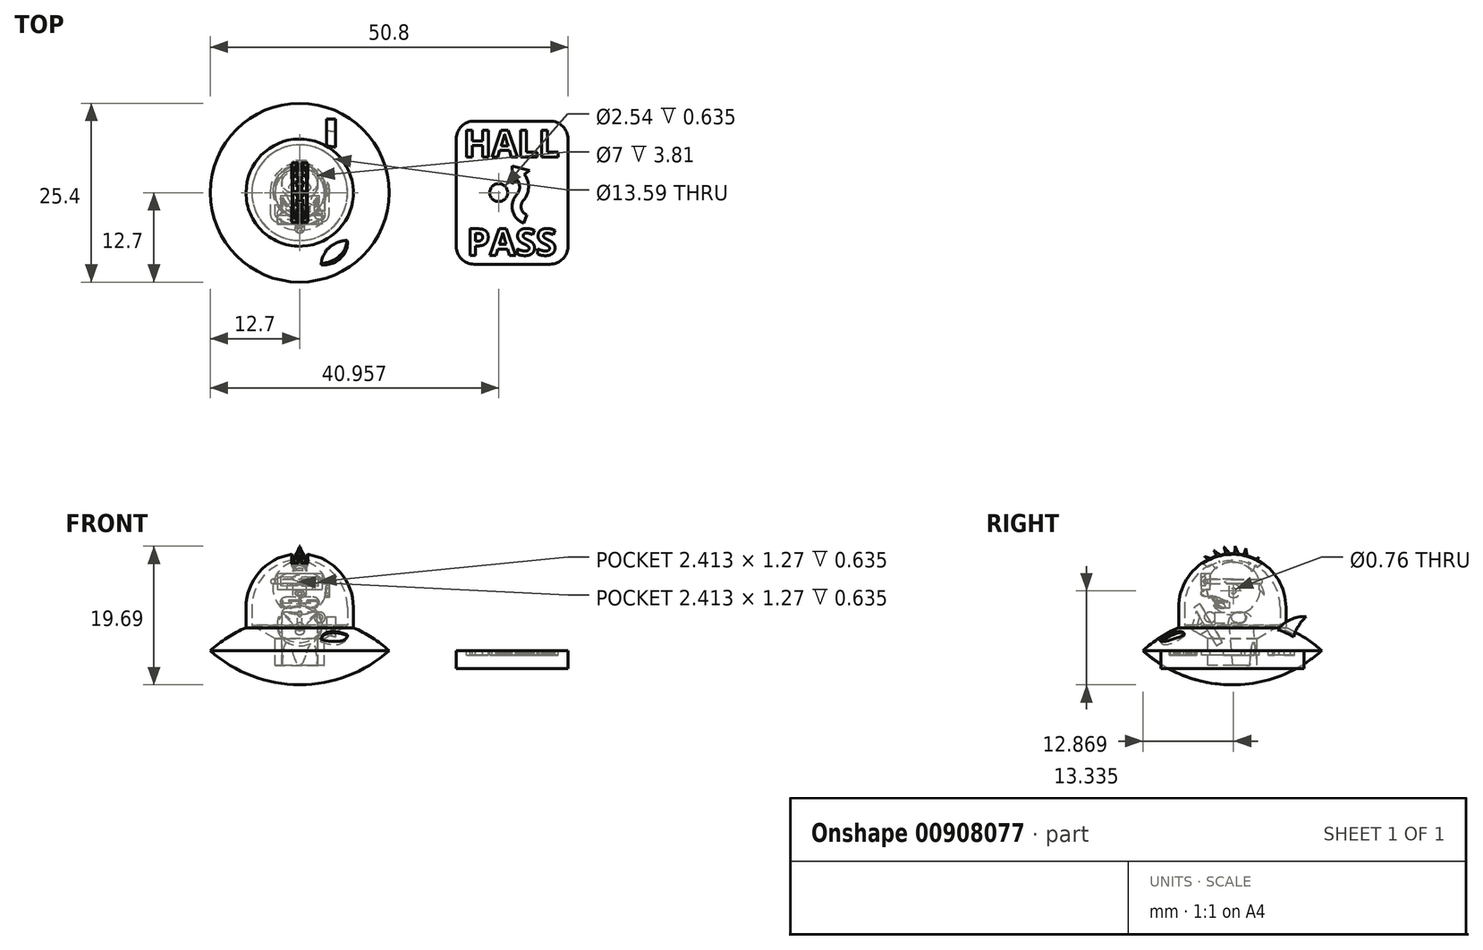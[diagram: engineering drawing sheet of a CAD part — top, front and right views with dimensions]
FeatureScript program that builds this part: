
annotation { "Feature Type Name" : "Feature", "Feature Type Description" : "" }
export const myFeature = defineFeature(function(context is Context, id is Id, definition is map)
    precondition{}
    {
        {
            var Q0;
            Q0=qCreatedBy(makeId("Right.planeOp"),FACE);
            var sketch = newSketch(context, id + "F0", { "sketchPlane" : qUnion([Q0])});
            skArc(sketch, "E0", {"start": v(-12.7, 0) * mm, "mid": v(-6.8, -3.6) * mm, "end": v(0, -4.85) * mm});
            skLineSegment(sketch, "E1", {"start": v(0, 0) * mm, "end": v(-43.2, 0) * mm, "construction": true});
            skArc(sketch, "E2.MirrorC", {"start": v(-12.7, 0) * mm, "mid": v(-9.91, 2.07) * mm, "end": v(-6.8, 3.6) * mm});
            skPoint(sketch, "E3", {"position": v(-12.7, 0) * mm});
            skPoint(sketch, "E4", {"position": v(12.7, 0) * mm});
            skLineSegment(sketch, "E5", {"start": v(0, -2.12) * mm, "end": v(0, -4.85) * mm});
            skLineSegment(sketch, "E6", {"start": v(-6.8, 3.6) * mm, "end": v(-3.5, 1.7) * mm});
            skLineSegment(sketch, "E7", {"start": v(-3.5, 1.7) * mm, "end": v(-3.5, -2.12) * mm});
            skLineSegment(sketch, "E8", {"start": v(-3.5, -2.12) * mm, "end": v(0, -2.12) * mm});
            skPoint(sketch, "E9.orphan", {"position": v(0, 4.85) * mm});
            skSolve(sketch);
        }
        {
            var Q0;
            Q0 = qSketchRegion(id + "F0", true);
            var Q1;
            Q1=sQuery(id+"F0.wireOp",EDGE,"E5");
            revolve(context, id + "F1", {"surfaceOperationType" : NewSurfaceOperationType.NEW, "entities" : qUnion([Q0]), "axis" : qUnion([Q1]), "revolveType" : RevolveType.FULL});
        }
        {
            var Q0;
            Q0=qCreatedBy(makeId("Right.planeOp"),FACE);
            cPlane(context, id + "F2", {"entities" : qUnion([Q0]), "cplaneType" : CPlaneType.OFFSET, "offset" : 5.08 * mm, "width" : 152.4 * mm, "height" : 152.4 * mm});
        }
        {
            var Q0;
            Q0=qCreatedBy(id+"F2.planeOp",FACE);
            var sketch = newSketch(context, id + "F3", { "sketchPlane" : qUnion([Q0])});
            skLineSegment(sketch, "E10", {"start": v(6.35, 2.86) * mm, "end": v(8.65, 1.78) * mm});
            skArc(sketch, "E11", {"start": v(10.47, 4.82) * mm, "mid": v(8.16, 4.36) * mm, "end": v(6.35, 2.86) * mm});
            skArc(sketch, "E12", {"start": v(10.47, 4.82) * mm, "mid": v(9.35, 3.42) * mm, "end": v(8.65, 1.78) * mm});
            skSolve(sketch);
        }
        {
            var Q0;
            Q0 = qSketchRegion(id + "F3", true);
            extrude(context, id + "F4", {"entities" : qUnion([Q0]), "operationType" : NewBodyOperationType.ADD, "oppositeDirection" : true, "depth" : 1.27 * mm, "offsetDistance" : 25.4 * mm});
        }
        {
            var Q0;
            Q0=sQuery(id+"F0.wireOp",EDGE,"E5");
            var Q1;
            Q1=qCreatedBy(makeId("Right.planeOp"),FACE);
            cPlane(context, id + "F5", {"entities" : qUnion([Q0, Q1]), "cplaneType" : CPlaneType.LINE_ANGLE, "offset" : 25.4 * mm, "angle" : 60 * degree, "width" : 152.4 * mm, "height" : 152.4 * mm});
        }
        {
            var Q0;
            Q0=qCreatedBy(id+"F5.planeOp",FACE);
            cPlane(context, id + "F6", {"entities" : qUnion([Q0]), "cplaneType" : CPlaneType.OFFSET, "offset" : 12.7 * mm, "oppositeDirection" : true, "width" : 152.4 * mm, "height" : 152.4 * mm});
        }
        {
            var Q0;
            Q0=qCreatedBy(id+"F6.planeOp",FACE);
            var sketch = newSketch(context, id + "F7", { "sketchPlane" : qUnion([Q0])});
            skLineSegment(sketch, "E13", {"start": v(0, 0) * mm, "end": v(0, 3.6) * mm, "construction": true});
            skLineSegment(sketch, "E14", {"start": v(4.4, 0) * mm, "end": v(-4.14, 0) * mm, "construction": true});
            skSolve(sketch);
        }
        {
            var Q0;
            Q0=sQuery(id+"F7.wireOp",EDGE,"E14");
            var Q1;
            Q1=qCreatedBy(id+"F6.planeOp",FACE);
            cPlane(context, id + "F8", {"entities" : qUnion([Q0, Q1]), "cplaneType" : CPlaneType.LINE_ANGLE, "offset" : 25.4 * mm, "angle" : 50 * degree, "oppositeDirection" : true, "width" : 152.4 * mm, "height" : 152.4 * mm});
        }
        {
            var Q0;
            Q0=qCreatedBy(id+"F8.planeOp",FACE);
            var sketch = newSketch(context, id + "F9", { "sketchPlane" : qUnion([Q0])});
            skLineSegment(sketch, "E15", {"start": v(3.94, -8.9) * mm, "end": v(1.17, -2.65) * mm, "construction": true});
            skLineSegment(sketch, "E16", {"start": v(2.55, -5.77) * mm, "end": v(6.21, -10.31) * mm, "construction": true});
            skLineSegment(sketch, "E17", {"start": v(2.55, -5.77) * mm, "end": v(-0.5, -2) * mm, "construction": true});
            skArc(sketch, "E18", {"start": v(4.53, -4.18) * mm, "mid": v(1.76, -4.78) * mm, "end": v(0.58, -7.37) * mm});
            skArc(sketch, "E19", {"start": v(0.58, -7.37) * mm, "mid": v(3.35, -6.76) * mm, "end": v(4.53, -4.18) * mm});
            skSolve(sketch);
        }
        {
            var Q0;
            Q0 = qSketchRegion(id + "F9", true);
            extrude(context, id + "F10", {"entities" : qUnion([Q0]), "operationType" : NewBodyOperationType.REMOVE, "oppositeDirection" : true, "depth" : 0.64 * mm, "offsetDistance" : 25.4 * mm});
        }
        {
            var Q0;
            Q0=qCreatedBy(makeId("Right.planeOp"),FACE);
            var sketch = newSketch(context, id + "F11", { "sketchPlane" : qUnion([Q0])});
            skLineSegment(sketch, "E20", {"start": v(-5.15, 2.64) * mm, "end": v(0.48, 5.9) * mm, "construction": true});
            skLineSegment(sketch, "E21", {"start": v(-5.15, 2.64) * mm, "end": v(-7.02, 1.56) * mm, "construction": true});
            skLineSegment(sketch, "E22", {"start": v(-5.47, 2.46) * mm, "end": v(-5.78, 3.01) * mm});
            skLineSegment(sketch, "E23", {"start": v(-5.78, 3.01) * mm, "end": v(-4.13, 3.96) * mm});
            skLineSegment(sketch, "E24", {"start": v(-4.13, 3.96) * mm, "end": v(-5.4, 6.16) * mm});
            skLineSegment(sketch, "E25", {"start": v(-5.4, 6.16) * mm, "end": v(-4.58, 6.64) * mm});
            skLineSegment(sketch, "E26", {"start": v(-4.58, 6.64) * mm, "end": v(-3, 3.89) * mm});
            skLineSegment(sketch, "E27", {"start": v(-5.47, 2.46) * mm, "end": v(-3, 3.89) * mm});
            skSolve(sketch);
        }
        {
            var Q0;
            Q0 = qSketchRegion(id + "F11", true);
            var Q1;
            Q1=sQuery(id+"F11.wireOp",EDGE,"E20");
            revolve(context, id + "F12", {"operationType" : NewBodyOperationType.ADD, "surfaceOperationType" : NewSurfaceOperationType.NEW, "entities" : qUnion([Q0]), "axis" : qUnion([Q1]), "revolveType" : RevolveType.FULL});
        }
        {
            var Q0;
            Q0=qCreatedBy(makeId("Right.planeOp"),FACE);
            var sketch = newSketch(context, id + "F13", { "sketchPlane" : qUnion([Q0])});
            skLineSegment(sketch, "E28", {"start": v(-4.78, 5.53) * mm, "end": v(-5.5, 2.85) * mm});
            skLineSegment(sketch, "E29.MirrorCS", {"start": v(-5.21, 2.68) * mm, "end": v(-4.47, 5.45) * mm});
            skLineSegment(sketch, "E30.MirrorCS", {"start": v(-4.47, 5.45) * mm, "end": v(-4.78, 5.53) * mm});
            skPoint(sketch, "E31.start.orphan", {"position": v(-5.09, 5.61) * mm});
            skLineSegment(sketch, "E32", {"start": v(-5.21, 2.68) * mm, "end": v(-5.52, 2.76) * mm});
            skLineSegment(sketch, "E33", {"start": v(-5.5, 2.85) * mm, "end": v(-5.52, 2.76) * mm});
            skSolve(sketch);
        }
        {
            var Q0;
            Q0 = qSketchRegion(id + "F13", true);
            var Q1;
            Q1=sQuery(id+"F13.wireOp",EDGE,"E28");
            revolve(context, id + "F14", {"operationType" : NewBodyOperationType.ADD, "surfaceOperationType" : NewSurfaceOperationType.NEW, "entities" : qUnion([Q0]), "axis" : qUnion([Q1]), "revolveType" : RevolveType.FULL});
        }
        {
            var Q0;
            Q0=qCreatedBy(makeId("Right.planeOp"),FACE);
            var sketch = newSketch(context, id + "F15", { "sketchPlane" : qUnion([Q0])});
            skLineSegment(sketch, "E34", {"start": v(0, 0) * mm, "end": v(0, 26.54) * mm, "construction": true});
            skArc(sketch, "E35", {"start": v(0, 12.93) * mm, "mid": v(-4.8, 10.94) * mm, "end": v(-6.8, 6.14) * mm});
            skLineSegment(sketch, "E36", {"start": v(-6.8, 6.14) * mm, "end": v(-6.8, 3.6) * mm});
            skArc(sketch, "E37", {"start": v(-7.62, 6.14) * mm, "mid": v(-5.39, 11.53) * mm, "end": v(0, 13.76) * mm});
            skLineSegment(sketch, "E38", {"start": v(-7.62, 6.14) * mm, "end": v(-7.62, 3.26) * mm});
            skLineSegment(sketch, "E39", {"start": v(-7.62, 3.26) * mm, "end": v(-6.8, 3.6) * mm});
            skLineSegment(sketch, "E40", {"start": v(0, 13.76) * mm, "end": v(0, 12.93) * mm});
            skSolve(sketch);
        }
        {
            var Q0;
            Q0 = qSketchRegion(id + "F15", true);
            var Q1;
            Q1=sQuery(id+"F15.wireOp",EDGE,"E34");
            revolve(context, id + "F16", {"surfaceOperationType" : NewSurfaceOperationType.NEW, "entities" : qUnion([Q0]), "axis" : qUnion([Q1]), "revolveType" : RevolveType.FULL});
        }
        {
            var Q0;
            Q0=qCreatedBy(makeId("Top.planeOp"),FACE);
            var sketch = newSketch(context, id + "F17", { "sketchPlane" : qUnion([Q0])});
            skLineSegment(sketch, "E41", {"start": v(0, 0) * mm, "end": v(38.1, 0) * mm, "construction": true});
            skLineSegment(sketch, "E42", {"start": v(38.1, 0) * mm, "end": v(38.1, 10.16) * mm});
            skLineSegment(sketch, "E43", {"start": v(38.1, 10.16) * mm, "end": v(22.23, 10.16) * mm});
            skLineSegment(sketch, "E44", {"start": v(22.23, 10.16) * mm, "end": v(22.23, 0) * mm});
            skLineSegment(sketch, "E45.MirrorCS", {"start": v(22.23, -10.16) * mm, "end": v(22.23, 0) * mm});
            skLineSegment(sketch, "E46.MirrorCS", {"start": v(38.1, -10.16) * mm, "end": v(22.23, -10.16) * mm});
            skLineSegment(sketch, "E47.MirrorCS", {"start": v(38.1, 0) * mm, "end": v(38.1, -10.16) * mm});
            skLineSegment(sketch, "E48", {"start": v(30.16, 10.16) * mm, "end": v(30.16, -10.16) * mm, "construction": true});
            skSolve(sketch);
        }
        {
            var Q0;
            Q0 = qSketchRegion(id + "F17", true);
            extrude(context, id + "F18", {"entities" : qUnion([Q0]), "oppositeDirection" : true, "depth" : 2.54 * mm, "offsetDistance" : 25.4 * mm});
        }
        {
            var Q0;
            Q0=qCreatedBy(makeId("Top.planeOp"),FACE);
            var sketch = newSketch(context, id + "F19", { "sketchPlane" : qUnion([Q0])});
            skLineSegment(sketch, "E49", {"start": v(30.16, 10.16) * mm, "end": v(30.16, -10.16) * mm, "construction": true});
            skText(sketch, "E50", { "text": "HALL", "fontName": "OpenSans-Bold.ttf"});
            skText(sketch, "E51", { "text": "PASS", "fontName": "OpenSans-Bold.ttf"});
            const initialGuessF19  = {"E50": [0.02324, 0.00508, 1, 0, 0.0038], "E51": [0.0237, -0.0089, 1, 0, 0.0038]};
            skSetInitialGuess(sketch, initialGuessF19);
            skSolve(sketch);
        }
        {
            var Q0;
            Q0 = qSketchRegion(id + "F19", true);
            extrude(context, id + "F20", {"entities" : qUnion([Q0]), "operationType" : NewBodyOperationType.REMOVE, "oppositeDirection" : true, "depth" : 0.64 * mm, "offsetDistance" : 25.4 * mm});
        }
        {
            var Q0;
            Q0=qCreatedBy(makeId("Top.planeOp"),FACE);
            var sketch = newSketch(context, id + "F21", { "sketchPlane" : qUnion([Q0])});
            skLineSegment(sketch, "E52", {"start": v(30.16, 10.16) * mm, "end": v(30.16, -10.16) * mm, "construction": true});
            skLineSegment(sketch, "E53", {"start": v(30.16, 3.81) * mm, "end": v(30.16, 1.27) * mm});
            skLineSegment(sketch, "E54", {"start": v(30.16, 3.81) * mm, "end": v(32.62, 3.15) * mm});
            skLineSegment(sketch, "E55", {"start": v(30.16, 3.81) * mm, "end": v(31.39, 2.21) * mm, "construction": true});
            skCircle(sketch, "E56", {"center": v(28.26, 0) * mm, "radius": 1.27 * mm});
            skLineSegment(sketch, "E57", {"start": v(30.16, 1.27) * mm, "end": v(32.62, 3.15) * mm});
            skLineSegment(sketch, "E58", {"start": v(30.89, 1.82) * mm, "end": v(34.6, -3) * mm, "construction": true});
            skLineSegment(sketch, "E59.MirrorCS", {"start": v(31.9, 2.6) * mm, "end": v(35.6, -2.23) * mm, "construction": true});
            skLineSegment(sketch, "E60", {"start": v(30.16, 1.27) * mm, "end": v(24.5, -3.08) * mm, "construction": true});
            skArc(sketch, "E61", {"start": v(30.8, -0.28) * mm, "mid": v(30.24, -2.6) * mm, "end": v(31.83, -4.36) * mm});
            skArc(sketch, "E62.trimOffspring", {"start": v(30.8, -0.28) * mm, "mid": v(31.23, 0.76) * mm, "end": v(30.89, 1.82) * mm});
            skArc(sketch, "E63", {"start": v(31.9, 2.6) * mm, "mid": v(32.5, 0.71) * mm, "end": v(31.75, -1.13) * mm});
            skArc(sketch, "E64", {"start": v(31.75, -1.13) * mm, "mid": v(31.47, -2.28) * mm, "end": v(32.27, -3.16) * mm});
            skLineSegment(sketch, "E65", {"start": v(32.27, -3.16) * mm, "end": v(31.83, -4.36) * mm});
            skSolve(sketch);
        }
        {
            var Q0;
            Q0=makeQuery(id+"F21.imprint","IMPRINT",FACE,{"disambiguationData":[TD([[makeQuery(id+"F21.imprint","IMPRINT",EDGE,{"derivedFrom":sQuery(id+"F21.wireOp",EDGE,"E56")}),1.0]])]});
            var Q1;
            {var subQ3=sQuery(id+"F21.wireOp",EDGE,"E53");Q1=makeQuery(id+"F21.imprint","IMPRINT",FACE,{"disambiguationData":[TD([[makeQuery(id+"F21.imprint","IMPRINT",EDGE,{"derivedFrom":subQ3}),1.0]])]});}
            var Q2;
            Q2=makeQuery(id+"F21.imprint","IMPRINT",FACE,{"disambiguationData":[TD([[makeQuery(id+"F21.imprint","IMPRINT",EDGE,{"derivedFrom":sQuery(id+"F21.wireOp",EDGE,"E61")}),1.0]])]});
            extrude(context, id + "F22", {"entities" : qUnion([Q0, Q1, Q2]), "operationType" : NewBodyOperationType.REMOVE, "oppositeDirection" : true, "depth" : 0.64 * mm, "offsetDistance" : 25.4 * mm});
        }
        {
            var Q0;
            Q0=makeQuery(id+"F18.opExtrude","SWEPT_EDGE",EDGE,{"disambiguationData":[OSD([sQuery(id+"F17.wireOp",EDGE,"E43"),sQuery(id+"F17.wireOp",EDGE,"E44")])]});
            var Q1;
            Q1=makeQuery(id+"F18.opExtrude","SWEPT_EDGE",EDGE,{"disambiguationData":[OSD([sQuery(id+"F17.wireOp",EDGE,"E42"),sQuery(id+"F17.wireOp",EDGE,"E43")])]});
            var Q2;
            Q2=makeQuery(id+"F18.opExtrude","SWEPT_EDGE",EDGE,{"disambiguationData":[OSD([sQuery(id+"F17.wireOp",EDGE,"E45.MirrorCS"),sQuery(id+"F17.wireOp",EDGE,"E46.MirrorCS")])]});
            var Q3;
            Q3=makeQuery(id+"F18.opExtrude","SWEPT_EDGE",EDGE,{"disambiguationData":[OSD([sQuery(id+"F17.wireOp",EDGE,"E46.MirrorCS"),sQuery(id+"F17.wireOp",EDGE,"E47.MirrorCS")])]});
            fillet(context, id + "F23", {"entities" : qUnion([Q0, Q1, Q2, Q3]), "radius" : 2.54 * mm, "tangentPropagation" : true, "allowEdgeOverflow" : false});
        }
        {
            var Q0;
            Q0=qCreatedBy(makeId("Right.planeOp"),FACE);
            var sketch = newSketch(context, id + "F24", { "sketchPlane" : qUnion([Q0])});
            skLineSegment(sketch, "E66", {"start": v(3.5, -2.12) * mm, "end": v(0, -2.12) * mm});
            skLineSegment(sketch, "E67", {"start": v(3.5, -2.12) * mm, "end": v(2.84, 5.47) * mm});
            skLineSegment(sketch, "E68", {"start": v(2.84, 5.47) * mm, "end": v(-0.66, 5.47) * mm});
            skLineSegment(sketch, "E69", {"start": v(-0.66, 5.47) * mm, "end": v(0, -2.12) * mm});
            skSolve(sketch);
        }
        {
            var Q0;
            Q0 = qSketchRegion(id + "F24", true);
            extrude(context, id + "F25", {"entities" : qUnion([Q0]), "operationType" : NewBodyOperationType.ADD, "endBound" : BoundingType.SYMMETRIC, "depth" : 5.08 * mm, "offsetDistance" : 25.4 * mm});
        }
        {
            var Q0;
            Q0=makeQuery(id+"F25.opExtrude","SWEPT_EDGE",EDGE,{"disambiguationData":[OSD([sQuery(id+"F24.wireOp",EDGE,"E68"),sQuery(id+"F24.wireOp",EDGE,"E69")])]});
            var Q1;
            Q1=makeQuery(id+"F25.opExtrude","SWEPT_EDGE",EDGE,{"disambiguationData":[OSD([sQuery(id+"F24.wireOp",EDGE,"E67"),sQuery(id+"F24.wireOp",EDGE,"E68")])]});
            var Q2;
            Q2=makeQuery(id+"F25.opExtrude","CAP_EDGE",EDGE,{"disambiguationData":[OSD([sQuery(id+"F24.wireOp",EDGE,"E69")])],"isStart":true});
            var Q3;
            Q3=makeQuery(id+"F25.opExtrude","CAP_EDGE",EDGE,{"disambiguationData":[OSD([sQuery(id+"F24.wireOp",EDGE,"E69")])],"isStart":false});
            var Q4;
            Q4=makeQuery(id+"F25.opExtrude","CAP_EDGE",EDGE,{"disambiguationData":[OSD([sQuery(id+"F24.wireOp",EDGE,"E67")])],"isStart":true});
            var Q5;
            Q5=makeQuery(id+"F25.opExtrude","CAP_EDGE",EDGE,{"disambiguationData":[OSD([sQuery(id+"F24.wireOp",EDGE,"E67")])],"isStart":false});
            fillet(context, id + "F26", {"entities" : qUnion([Q0, Q1, Q2, Q3, Q4, Q5]), "radius" : 1.52 * mm, "tangentPropagation" : true, "allowEdgeOverflow" : false});
        }
        {
            var Q0;
            Q0=qCreatedBy(makeId("Right.planeOp"),FACE);
            cPlane(context, id + "F27", {"entities" : qUnion([Q0]), "cplaneType" : CPlaneType.OFFSET, "offset" : 2.86 * mm, "width" : 152.4 * mm, "height" : 152.4 * mm});
        }
        {
            var Q0;
            Q0=qCreatedBy(id+"F27.planeOp",FACE);
            var sketch = newSketch(context, id + "F28", { "sketchPlane" : qUnion([Q0])});
            skLineSegment(sketch, "E70", {"start": v(1.27, 4.71) * mm, "end": v(-2.54, 4.71) * mm});
            skLineSegment(sketch, "E71", {"start": v(1.27, 5.47) * mm, "end": v(1.27, 4.71) * mm});
            skLineSegment(sketch, "E72", {"start": v(1.27, 5.47) * mm, "end": v(-2.54, 5.47) * mm});
            skLineSegment(sketch, "E73", {"start": v(-2.54, 4.71) * mm, "end": v(-2.54, 5.47) * mm});
            skSolve(sketch);
        }
        {
            var Q0;
            Q0 = qSketchRegion(id + "F28", true);
            var Q1;
            Q1=sQuery(id+"F28.wireOp",EDGE,"E70");
            revolve(context, id + "F29", {"operationType" : NewBodyOperationType.ADD, "surfaceOperationType" : NewSurfaceOperationType.NEW, "entities" : qUnion([Q0]), "axis" : qUnion([Q1]), "revolveType" : RevolveType.FULL});
        }
        {
            var Q0;
            Q0=makeQuery(id+"F29.opRevolve","SWEPT_FACE",FACE,{"disambiguationData":[OSD([sQuery(id+"F28.wireOp",EDGE,"E71")])]});
            var sketch = newSketch(context, id + "F30", { "sketchPlane" : qUnion([Q0])});
            skArc(sketch, "E74", {"start": v(-2.86, 5.47) * mm, "mid": v(-3.62, 4.71) * mm, "end": v(-2.86, 3.95) * mm});
            skLineSegment(sketch, "E75", {"start": v(-2.86, 5.47) * mm, "end": v(-2.86, 3.95) * mm});
            skSolve(sketch);
        }
        {
            var Q0;
            Q0=makeQuery(id+"F30.imprint","IMPRINT",FACE,{"disambiguationData":[TD([[makeQuery(id+"F30.imprint","IMPRINT",EDGE,{"derivedFrom":sQuery(id+"F30.wireOp",EDGE,"E74")}),1.0]])]});
            var Q1;
            Q1=sQuery(id+"F30.wireOp",EDGE,"E75");
            revolve(context, id + "F31", {"operationType" : NewBodyOperationType.ADD, "surfaceOperationType" : NewSurfaceOperationType.NEW, "entities" : qUnion([Q0]), "axis" : qUnion([Q1]), "revolveType" : RevolveType.FULL});
        }
        {
            var Q0;
            Q0=qCreatedBy(id+"F27.planeOp",FACE);
            var sketch = newSketch(context, id + "F32", { "sketchPlane" : qUnion([Q0])});
            skLineSegment(sketch, "E76", {"start": v(-2.54, 4.71) * mm, "end": v(-7.1, 4.71) * mm, "construction": true});
            skArc(sketch, "E77", {"start": v(-2.41, 4.71) * mm, "mid": v(-3.18, 5.47) * mm, "end": v(-3.94, 4.71) * mm});
            skLineSegment(sketch, "E78", {"start": v(-3.94, 4.71) * mm, "end": v(-2.41, 4.71) * mm});
            skSolve(sketch);
        }
        {
            var Q0;
            Q0=makeQuery(id+"F32.imprint","IMPRINT",FACE,{"disambiguationData":[TD([[makeQuery(id+"F32.imprint","IMPRINT",EDGE,{"derivedFrom":sQuery(id+"F32.wireOp",EDGE,"E77")}),1.0]])]});
            var Q1;
            Q1=sQuery(id+"F32.wireOp",EDGE,"E78");
            revolve(context, id + "F33", {"operationType" : NewBodyOperationType.ADD, "surfaceOperationType" : NewSurfaceOperationType.NEW, "entities" : qUnion([Q0]), "axis" : qUnion([Q1]), "revolveType" : RevolveType.FULL});
        }
        {
            var Q0;
            Q0=qCreatedBy(makeId("Right.planeOp"),FACE);
            var sketch = newSketch(context, id + "F34", { "sketchPlane" : qUnion([Q0])});
            skLineSegment(sketch, "E79", {"start": v(1.16, 5.21) * mm, "end": v(-0.82, 12.57) * mm});
            skArc(sketch, "E80", {"start": v(-0.82, 12.57) * mm, "mid": v(-3.51, 7.9) * mm, "end": v(1.16, 5.21) * mm});
            skLineSegment(sketch, "E81", {"start": v(1.16, 5.47) * mm, "end": v(1.16, 3.84) * mm, "construction": true});
            skSolve(sketch);
        }
        {
            var Q0;
            Q0=makeQuery(id+"F34.imprint","IMPRINT",FACE,{"disambiguationData":[TD([[makeQuery(id+"F34.imprint","IMPRINT",EDGE,{"derivedFrom":sQuery(id+"F34.wireOp",EDGE,"E79")}),1.0]])]});
            var Q1;
            Q1=sQuery(id+"F34.wireOp",EDGE,"E79");
            revolve(context, id + "F35", {"operationType" : NewBodyOperationType.ADD, "surfaceOperationType" : NewSurfaceOperationType.NEW, "entities" : qUnion([Q0]), "axis" : qUnion([Q1]), "revolveType" : RevolveType.FULL});
        }
        {
            var Q0;
            Q0=qCreatedBy(makeId("Front.planeOp"),FACE);
            cPlane(context, id + "F36", {"entities" : qUnion([Q0]), "cplaneType" : CPlaneType.OFFSET, "offset" : 3.17 * mm, "width" : 152.4 * mm, "height" : 152.4 * mm});
        }
        {
            var Q0;
            Q0=qCreatedBy(id+"F36.planeOp",FACE);
            var sketch = newSketch(context, id + "F37", { "sketchPlane" : qUnion([Q0])});
            skLineSegment(sketch, "E82", {"start": v(0, 6.66) * mm, "end": v(0, 16.17) * mm, "construction": true});
            skLineSegment(sketch, "E83", {"start": v(0, 10.96) * mm, "end": v(-3.18, 10.96) * mm});
            skLineSegment(sketch, "E84", {"start": v(-3.18, 10.96) * mm, "end": v(-3.18, 8.67) * mm});
            skLineSegment(sketch, "E85", {"start": v(-3.18, 8.67) * mm, "end": v(0, 8.67) * mm});
            skLineSegment(sketch, "E86.MirrorCS", {"start": v(0, 10.96) * mm, "end": v(3.17, 10.96) * mm});
            skLineSegment(sketch, "E87.MirrorCS", {"start": v(3.18, 10.96) * mm, "end": v(3.18, 8.67) * mm});
            skLineSegment(sketch, "E88.MirrorCS", {"start": v(3.18, 8.67) * mm, "end": v(0, 8.67) * mm});
            skLineSegment(sketch, "E89.bottom", {"start": v(-2.67, 10.45) * mm, "end": v(-0.25, 10.45) * mm});
            skLineSegment(sketch, "E89.top", {"start": v(-2.67, 9.18) * mm, "end": v(-0.25, 9.18) * mm});
            skLineSegment(sketch, "E89.left", {"start": v(-2.67, 10.45) * mm, "end": v(-2.67, 9.18) * mm});
            skLineSegment(sketch, "E89.right", {"start": v(-0.25, 10.45) * mm, "end": v(-0.25, 9.18) * mm});
            skLineSegment(sketch, "E90.MirrorCS", {"start": v(2.67, 10.45) * mm, "end": v(0.25, 10.45) * mm});
            skLineSegment(sketch, "E91.MirrorCS", {"start": v(0.25, 10.45) * mm, "end": v(0.25, 9.18) * mm});
            skLineSegment(sketch, "E92.MirrorCS", {"start": v(2.67, 9.18) * mm, "end": v(0.25, 9.18) * mm});
            skLineSegment(sketch, "E93.MirrorCS", {"start": v(2.67, 10.45) * mm, "end": v(2.67, 9.18) * mm});
            skEllipse(sketch, "E94", {"center": v(0, 8.16) * mm, "majorRadius": 0.64 * mm, "minorRadius": 0.44 * mm, "majorAxis": v(1, 0)});
            skSolve(sketch);
        }
        {
            var Q0;
            Q0 = qSketchRegion(id + "F37", true);
            var Q1;
            Q1=makeQuery(id+"F37.imprint","IMPRINT",FACE,{"disambiguationData":[TD([[makeQuery(id+"F37.imprint","IMPRINT",EDGE,{"derivedFrom":sQuery(id+"F37.wireOp",EDGE,"E89.bottom")}),-1.0]])]});
            var Q2;
            Q2=makeQuery(id+"F37.imprint","IMPRINT",FACE,{"disambiguationData":[TD([[makeQuery(id+"F37.imprint","IMPRINT",EDGE,{"derivedFrom":sQuery(id+"F37.wireOp",EDGE,"E90.MirrorCS")}),1.0]])]});
            extrude(context, id + "F38", {"entities" : qUnion([Q0, Q1, Q2]), "operationType" : NewBodyOperationType.ADD, "depth" : 1.27 * mm, "offsetDistance" : 25.4 * mm});
        }
        {
            var Q0;
            Q0=makeQuery(id+"F38.opExtrude","CAP_EDGE",EDGE,{"disambiguationData":[OSD([sQuery(id+"F37.wireOp",EDGE,"E94")])],"isStart":false});
            fillet(context, id + "F39", {"entities" : qUnion([Q0]), "radius" : 0.38 * mm, "tangentPropagation" : true, "allowEdgeOverflow" : false});
        }
        {
            var Q0;
            Q0=makeQuery(id+"F38.opExtrude","CAP_FACE",FACE,{"disambiguationData":[OSD([sQuery(id+"F37.wireOp",EDGE,"E83"),sQuery(id+"F37.wireOp",EDGE,"E84"),sQuery(id+"F37.wireOp",EDGE,"E85"),sQuery(id+"F37.wireOp",EDGE,"E86.MirrorCS"),sQuery(id+"F37.wireOp",EDGE,"E87.MirrorCS"),sQuery(id+"F37.wireOp",EDGE,"E88.MirrorCS")])],"isStart":false});
            var sketch = newSketch(context, id + "F40", { "sketchPlane" : qUnion([Q0])});
            skLineSegment(sketch, "E95", {"start": v(-2.67, 10.45) * mm, "end": v(-0.25, 10.45) * mm, "construction": true});
            skLineSegment(sketch, "E96", {"start": v(-0.25, 10.45) * mm, "end": v(-0.25, 9.18) * mm, "construction": true});
            skLineSegment(sketch, "E97", {"start": v(-0.25, 9.18) * mm, "end": v(-2.67, 9.18) * mm});
            skLineSegment(sketch, "E98", {"start": v(-2.67, 9.18) * mm, "end": v(-2.67, 10.45) * mm});
            skLineSegment(sketch, "E99.MirrorCS", {"start": v(2.67, 10.45) * mm, "end": v(0.25, 10.45) * mm, "construction": true});
            skLineSegment(sketch, "E100.MirrorCS", {"start": v(0.25, 10.45) * mm, "end": v(0.25, 9.18) * mm, "construction": true});
            skLineSegment(sketch, "E101.MirrorCS", {"start": v(0.25, 9.18) * mm, "end": v(2.67, 9.18) * mm});
            skLineSegment(sketch, "E102.MirrorCS", {"start": v(2.67, 9.18) * mm, "end": v(2.67, 10.45) * mm});
            skLineSegment(sketch, "E103", {"start": v(-0.25, 9.18) * mm, "end": v(-0.25, 9.81) * mm});
            skLineSegment(sketch, "E104", {"start": v(-0.25, 9.81) * mm, "end": v(-2.67, 10.45) * mm});
            skLineSegment(sketch, "E105", {"start": v(0.25, 9.18) * mm, "end": v(0.25, 9.81) * mm});
            skLineSegment(sketch, "E106", {"start": v(0.25, 9.81) * mm, "end": v(2.67, 10.45) * mm});
            skSolve(sketch);
        }
        {
            var Q0;
            Q0 = qSketchRegion(id + "F40", true);
            extrude(context, id + "F41", {"entities" : qUnion([Q0]), "operationType" : NewBodyOperationType.REMOVE, "oppositeDirection" : true, "depth" : 0.64 * mm, "offsetDistance" : 25.4 * mm});
        }
        {
            var Q0;
            Q0=makeQuery(id+"F38.opExtrude","SWEPT_FACE",FACE,{"disambiguationData":[OSD([sQuery(id+"F37.wireOp",EDGE,"E83"),sQuery(id+"F37.wireOp",EDGE,"E86.MirrorCS")])]});
            cPlane(context, id + "F42", {"entities" : qUnion([Q0]), "cplaneType" : CPlaneType.OFFSET, "offset" : 1.14 * mm, "oppositeDirection" : true, "width" : 152.4 * mm, "height" : 152.4 * mm});
        }
        {
            var Q0;
            Q0=qCreatedBy(id+"F42.planeOp",FACE);
            var sketch = newSketch(context, id + "F43", { "sketchPlane" : qUnion([Q0])});
            skLineSegment(sketch, "E107", {"start": v(0, -4.43) * mm, "end": v(0, 4.94) * mm, "construction": true});
            skArc(sketch, "E108", {"start": v(-3.8, -3.18) * mm, "mid": v(-3.62, -3.62) * mm, "end": v(-3.18, -3.81) * mm});
            skCircle(sketch, "E109", {"center": v(0, 0.15) * mm, "radius": 3.5 * mm, "construction": true});
            skLineSegment(sketch, "E110", {"start": v(-3.8, -3.18) * mm, "end": v(-3.8, 0.15) * mm});
            skArc(sketch, "E111", {"start": v(3.8, 0.15) * mm, "mid": v(0, 3.96) * mm, "end": v(-3.8, 0.15) * mm});
            skLineSegment(sketch, "E112.MirrorCS", {"start": v(3.8, -3.18) * mm, "end": v(3.8, 0.15) * mm});
            skPoint(sketch, "E113", {"position": v(-3.18, -3.81) * mm});
            skArc(sketch, "E114.MirrorCS", {"start": v(3.8, -3.18) * mm, "mid": v(3.62, -3.62) * mm, "end": v(3.18, -3.81) * mm});
            skArc(sketch, "E115.MirrorC", {"start": v(-3.8, 0.15) * mm, "mid": v(0, 3.96) * mm, "end": v(3.8, 0.15) * mm});
            skSolve(sketch);
        }
        {
            var Q0;
            Q0=makeQuery(id+"F38.opExtrude","SWEPT_FACE",FACE,{"disambiguationData":[OSD([sQuery(id+"F37.wireOp",EDGE,"E84")])]});
            var sketch = newSketch(context, id + "F44", { "sketchPlane" : qUnion([Q0])});
            skCircle(sketch, "E116", {"center": v(3.81, 9.81) * mm, "radius": 0.32 * mm});
            skSolve(sketch);
        }
        {
            var Q0;
            Q0=makeQuery(id+"F44.imprint","IMPRINT",FACE,{"disambiguationData":[TD([[makeQuery(id+"F44.imprint","IMPRINT",EDGE,{"derivedFrom":sQuery(id+"F44.wireOp",EDGE,"E116")}),1.0]])]});
            var Q1;
            Q1=sQuery(id+"F43.wireOp",EDGE,"E108");
            var Q2;
            Q2=sQuery(id+"F43.wireOp",EDGE,"E110");
            var Q3;
            Q3=sQuery(id+"F43.wireOp",EDGE,"E115.MirrorC");
            var Q4;
            Q4=sQuery(id+"F43.wireOp",EDGE,"E112.MirrorCS");
            var Q5;
            Q5=sQuery(id+"F43.wireOp",EDGE,"E114.MirrorCS");
            sweep(context, id + "F45", {"operationType" : NewBodyOperationType.ADD, "profiles" : qUnion([Q0]), "path" : qUnion([Q1, Q2, Q3, Q4, Q5])});
        }
        {
            var Q0;
            Q0=qCreatedBy(id+"F36.planeOp",FACE);
            var sketch = newSketch(context, id + "F46", { "sketchPlane" : qUnion([Q0])});
            skArc(sketch, "E117", {"start": v(-2.06, 7.64) * mm, "mid": v(-2.7, 6.6) * mm, "end": v(-1.58, 6.07) * mm});
            skLineSegment(sketch, "E118", {"start": v(0, 8.4) * mm, "end": v(0, 5.03) * mm, "construction": true});
            skArc(sketch, "E119", {"start": v(0, 7.47) * mm, "mid": v(-1.02, 7.7) * mm, "end": v(-2.06, 7.64) * mm});
            skArc(sketch, "E120", {"start": v(0, 6.4) * mm, "mid": v(-0.8, 6.3) * mm, "end": v(-1.58, 6.07) * mm});
            skArc(sketch, "E121.MirrorCS", {"start": v(0, 7.47) * mm, "mid": v(1.02, 7.7) * mm, "end": v(2.06, 7.64) * mm});
            skArc(sketch, "E122.MirrorCS", {"start": v(2.06, 7.64) * mm, "mid": v(2.7, 6.6) * mm, "end": v(1.58, 6.07) * mm});
            skArc(sketch, "E123.MirrorCS", {"start": v(0, 6.4) * mm, "mid": v(0.8, 6.3) * mm, "end": v(1.58, 6.07) * mm});
            skSolve(sketch);
        }
        {
            var Q0;
            Q0 = qSketchRegion(id + "F46", true);
            extrude(context, id + "F47", {"entities" : qUnion([Q0]), "operationType" : NewBodyOperationType.REMOVE, "oppositeDirection" : true, "depth" : 2.8 * mm, "offsetDistance" : 25.4 * mm});
        }
        {
            var Q0;
            Q0 = qSketchRegion(id + "F46", true);
            extrude(context, id + "F48", {"entities" : qUnion([Q0]), "operationType" : NewBodyOperationType.REMOVE, "depth" : 0.64 * mm, "offsetDistance" : 25.4 * mm});
        }
        {
            var Q0;
            Q0=qCreatedBy(makeId("Right.planeOp"),FACE);
            var sketch = newSketch(context, id + "F49", { "sketchPlane" : qUnion([Q0])});
            skArc(sketch, "E124", {"start": v(0.17, 12.32) * mm, "mid": v(-3.26, 8.9) * mm, "end": v(0.17, 5.46) * mm});
            skLineSegment(sketch, "E125", {"start": v(0.17, 12.32) * mm, "end": v(0.17, 5.46) * mm});
            skLineSegment(sketch, "E126", {"start": v(0.17, 8.9) * mm, "end": v(4.77, 8.9) * mm, "construction": true});
            skSolve(sketch);
        }
        {
            var Q0;
            Q0 = qSketchRegion(id + "F49", true);
            var Q1;
            Q1=sQuery(id+"F49.wireOp",EDGE,"E125");
            revolve(context, id + "F50", {"operationType" : NewBodyOperationType.ADD, "surfaceOperationType" : NewSurfaceOperationType.NEW, "entities" : qUnion([Q0]), "axis" : qUnion([Q1]), "revolveType" : RevolveType.FULL});
        }
        {
            var Q0;
            Q0=qCreatedBy(makeId("Right.planeOp"),FACE);
            cPlane(context, id + "F51", {"entities" : qUnion([Q0]), "cplaneType" : CPlaneType.OFFSET, "offset" : 3.56 * mm, "width" : 152.4 * mm, "height" : 152.4 * mm});
        }
        {
            var Q0;
            Q0=qCreatedBy(id+"F51.planeOp",FACE);
            var sketch = newSketch(context, id + "F52", { "sketchPlane" : qUnion([Q0])});
            skArc(sketch, "E127", {"start": v(0.17, 7.53) * mm, "mid": v(1.12, 8.48) * mm, "end": v(0.17, 9.44) * mm});
            skPoint(sketch, "E128.start.orphan", {"position": v(-0.47, 9.2) * mm});
            skArc(sketch, "E129", {"start": v(0.17, 9.44) * mm, "mid": v(-0.17, 9.37) * mm, "end": v(-0.47, 9.2) * mm});
            skArc(sketch, "E130", {"start": v(0.17, 7.53) * mm, "mid": v(-0.17, 7.6) * mm, "end": v(-0.47, 7.77) * mm});
            skLineSegment(sketch, "E131", {"start": v(-0.47, 9.2) * mm, "end": v(-0.47, 7.77) * mm});
            skCircle(sketch, "E132", {"center": v(0.17, 8.48) * mm, "radius": 0.38 * mm});
            skSolve(sketch);
        }
        {
            var Q0;
            Q0 = qSketchRegion(id + "F52", true);
            extrude(context, id + "F53", {"entities" : qUnion([Q0]), "operationType" : NewBodyOperationType.ADD, "depth" : 0.64 * mm, "offsetDistance" : 25.4 * mm});
        }
        {
            var Q0;
            Q0=qCreatedBy(makeId("Right.planeOp"),FACE);
            var sketch = newSketch(context, id + "F54", { "sketchPlane" : qUnion([Q0])});
            skArc(sketch, "E133", {"start": v(-0.52, 12.12) * mm, "mid": v(-1.33, 11.83) * mm, "end": v(-2.04, 11.34) * mm});
            skLineSegment(sketch, "E134", {"start": v(-0.52, 12.12) * mm, "end": v(-3.93, 13.38) * mm});
            skLineSegment(sketch, "E135", {"start": v(-3.93, 13.38) * mm, "end": v(-2.04, 11.34) * mm});
            skSolve(sketch);
        }
        {
            var Q0;
            Q0 = qSketchRegion(id + "F54", true);
            extrude(context, id + "F55", {"entities" : qUnion([Q0]), "endBound" : BoundingType.SYMMETRIC, "depth" : 1.9 * mm, "offsetDistance" : 25.4 * mm});
        }
        {
            var Q0;
            Q0=qCreatedBy(makeId("Right.planeOp"),FACE);
            var sketch = newSketch(context, id + "F56", { "sketchPlane" : qUnion([Q0])});
            skCircle(sketch, "E136", {"center": v(0.17, 8.9) * mm, "radius": 3.81 * mm, "construction": true});
            skArc(sketch, "E137.trimOffspring", {"start": v(4.54, 7.88) * mm, "mid": v(4.1, 8.44) * mm, "end": v(3.52, 8.87) * mm});
            skArc(sketch, "E138.trimOffspring", {"start": v(4.54, 7.88) * mm, "mid": v(4.2, 9.03) * mm, "end": v(3.37, 9.9) * mm});
            skArc(sketch, "E139.trimOffspring", {"start": v(3.52, 8.87) * mm, "mid": v(3.49, 9.39) * mm, "end": v(3.37, 9.9) * mm});
            skSolve(sketch);
        }
        {
            var Q0;
            Q0=makeQuery(id+"F56.imprint","IMPRINT",FACE,{"disambiguationData":[TD([[makeQuery(id+"F56.imprint","IMPRINT",EDGE,{"derivedFrom":sQuery(id+"F56.wireOp",EDGE,"E137.trimOffspring")}),-1.0]])]});
            extrude(context, id + "F57", {"entities" : qUnion([Q0]), "operationType" : NewBodyOperationType.ADD, "endBound" : BoundingType.SYMMETRIC, "depth" : 1.9 * mm, "offsetDistance" : 25.4 * mm});
        }
        {
            var Q0;
            Q0=qCreatedBy(makeId("Right.planeOp"),FACE);
            var sketch = newSketch(context, id + "F58", { "sketchPlane" : qUnion([Q0])});
            skCircle(sketch, "E140", {"center": v(0.17, 8.9) * mm, "radius": 3.43 * mm, "construction": true});
            skLineSegment(sketch, "E141", {"start": v(-2.7, 7.01) * mm, "end": v(-2.49, 7.15) * mm});
            skLineSegment(sketch, "E142", {"start": v(-2.35, 6.96) * mm, "end": v(-2.55, 6.8) * mm});
            skLineSegment(sketch, "E143", {"start": v(-2.55, 6.8) * mm, "end": v(-2.6, 6.76) * mm});
            skLineSegment(sketch, "E144", {"start": v(-2.6, 6.76) * mm, "end": v(-2.77, 6.97) * mm});
            skLineSegment(sketch, "E145", {"start": v(-2.77, 6.97) * mm, "end": v(-2.7, 7.01) * mm});
            skArc(sketch, "E146", {"start": v(-2.49, 7.15) * mm, "mid": v(-2.42, 7.06) * mm, "end": v(-2.35, 6.96) * mm});
            skSolve(sketch);
        }
        {
            var Q0;
            Q0 = qSketchRegion(id + "F58", true);
            var Q1;
            Q1=sQuery(id+"F49.wireOp",EDGE,"E125");
            revolve(context, id + "F59", {"operationType" : NewBodyOperationType.REMOVE, "surfaceOperationType" : NewSurfaceOperationType.NEW, "entities" : qUnion([Q0]), "axis" : qUnion([Q1]), "revolveType" : RevolveType.SYMMETRIC, "oppositeDirection" : true, "angle" : 140 * degree});
        }
        {
            var Q0;
            Q0=qCreatedBy(makeId("Right.planeOp"),FACE);
            var sketch = newSketch(context, id + "F60", { "sketchPlane" : qUnion([Q0])});
            skArc(sketch, "E147", {"start": v(-2.81, 7.8) * mm, "mid": v(-2.35, 6.96) * mm, "end": v(-1.65, 6.3) * mm});
            skArc(sketch, "E148", {"start": v(-3.05, 7.72) * mm, "mid": v(-2.55, 6.8) * mm, "end": v(-1.8, 6.09) * mm});
            skLineSegment(sketch, "E149", {"start": v(-2.81, 7.8) * mm, "end": v(-3.05, 7.72) * mm});
            skLineSegment(sketch, "E150", {"start": v(-1.65, 6.3) * mm, "end": v(-1.8, 6.09) * mm});
            skSolve(sketch);
        }
        {
            var Q0;
            Q0 = qSketchRegion(id + "F60", true);
            var Q1;
            Q1=sQuery(id+"F49.wireOp",EDGE,"E125");
            revolve(context, id + "F61", {"operationType" : NewBodyOperationType.REMOVE, "surfaceOperationType" : NewSurfaceOperationType.NEW, "entities" : qUnion([Q0]), "axis" : qUnion([Q1]), "revolveType" : RevolveType.SYMMETRIC, "oppositeDirection" : true, "angle" : 5 * degree});
        }
        {
            var Q0;
            Q0=qCreatedBy(makeId("Right.planeOp"),FACE);
            var sketch = newSketch(context, id + "F62", { "sketchPlane" : qUnion([Q0])});
            skCircle(sketch, "E151", {"center": v(0.17, 8.9) * mm, "radius": 3.56 * mm, "construction": true});
            skLineSegment(sketch, "E152", {"start": v(2, 11.94) * mm, "end": v(3.73, 13.23) * mm});
            skLineSegment(sketch, "E153", {"start": v(3.73, 13.23) * mm, "end": v(2.9, 11.17) * mm});
            skArc(sketch, "E154", {"start": v(2, 11.94) * mm, "mid": v(2.49, 11.6) * mm, "end": v(2.9, 11.17) * mm});
            skSolve(sketch);
        }
        {
            var Q0;
            Q0 = qSketchRegion(id + "F62", true);
            extrude(context, id + "F63", {"entities" : qUnion([Q0]), "endBound" : BoundingType.SYMMETRIC, "depth" : 1.9 * mm, "offsetDistance" : 25.4 * mm});
        }
        {
            var Q0;
            Q0=qCreatedBy(makeId("Front.planeOp"),FACE);
            var sketch = newSketch(context, id + "F64", { "sketchPlane" : qUnion([Q0])});
            skLineSegment(sketch, "E155", {"start": v(0, 34.37) * mm, "end": v(0, 44.83) * mm, "construction": true});
            skCircle(sketch, "E156", {"center": v(0, 8.9) * mm, "radius": 3.81 * mm, "construction": true});
            skLineSegment(sketch, "E157", {"start": v(0, 8.9) * mm, "end": v(0, 15.72) * mm, "construction": true});
            skLineSegment(sketch, "E158", {"start": v(-0.95, 12.58) * mm, "end": v(0, 14.96) * mm});
            skLineSegment(sketch, "E159.MirrorCS", {"start": v(0.95, 12.58) * mm, "end": v(0, 14.96) * mm});
            skLineSegment(sketch, "E160", {"start": v(-0.95, 12.58) * mm, "end": v(-1.36, 15.72) * mm});
            skLineSegment(sketch, "E161", {"start": v(-1.36, 15.72) * mm, "end": v(0, 15.72) * mm});
            skLineSegment(sketch, "E162.MirrorCS", {"start": v(0.95, 12.58) * mm, "end": v(1.36, 15.72) * mm});
            skLineSegment(sketch, "E163.MirrorCS", {"start": v(1.36, 15.72) * mm, "end": v(0, 15.72) * mm});
            skLineSegment(sketch, "E164", {"start": v(0, 8.89) * mm, "end": v(-2.25, 8.89) * mm, "construction": true});
            skSolve(sketch);
        }
        {
            var Q0;
            Q0 = qSketchRegion(id + "F64", true);
            var Q1;
            Q1=sQuery(id+"F64.wireOp",EDGE,"E164");
            revolve(context, id + "F65", {"operationType" : NewBodyOperationType.REMOVE, "surfaceOperationType" : NewSurfaceOperationType.NEW, "entities" : qUnion([Q0]), "axis" : qUnion([Q1]), "revolveType" : RevolveType.SYMMETRIC, "oppositeDirection" : true, "angle" : 100 * degree});
        }
        {
            var Q0;
            Q0=makeQuery(id+"F55.opExtrude","SWEPT_BODY",BODY,{"disambiguationData":[OSD([sQuery(id+"F54.wireOp",EDGE,"E133"),sQuery(id+"F54.wireOp",EDGE,"E134"),sQuery(id+"F54.wireOp",EDGE,"E135")])]});
            var Q1;
            Q1=sQuery(id+"F64.wireOp",EDGE,"E164");
            circularPattern(context, id + "F66", {"operationType" : NewBodyOperationType.ADD, "entities" : qUnion([Q0]), "axis" : qUnion([Q1]), "angle" : 60 * degree, "instanceCount" : 5, "equalSpace" : true, "fullFeaturePattern" : false});
        }
    });
